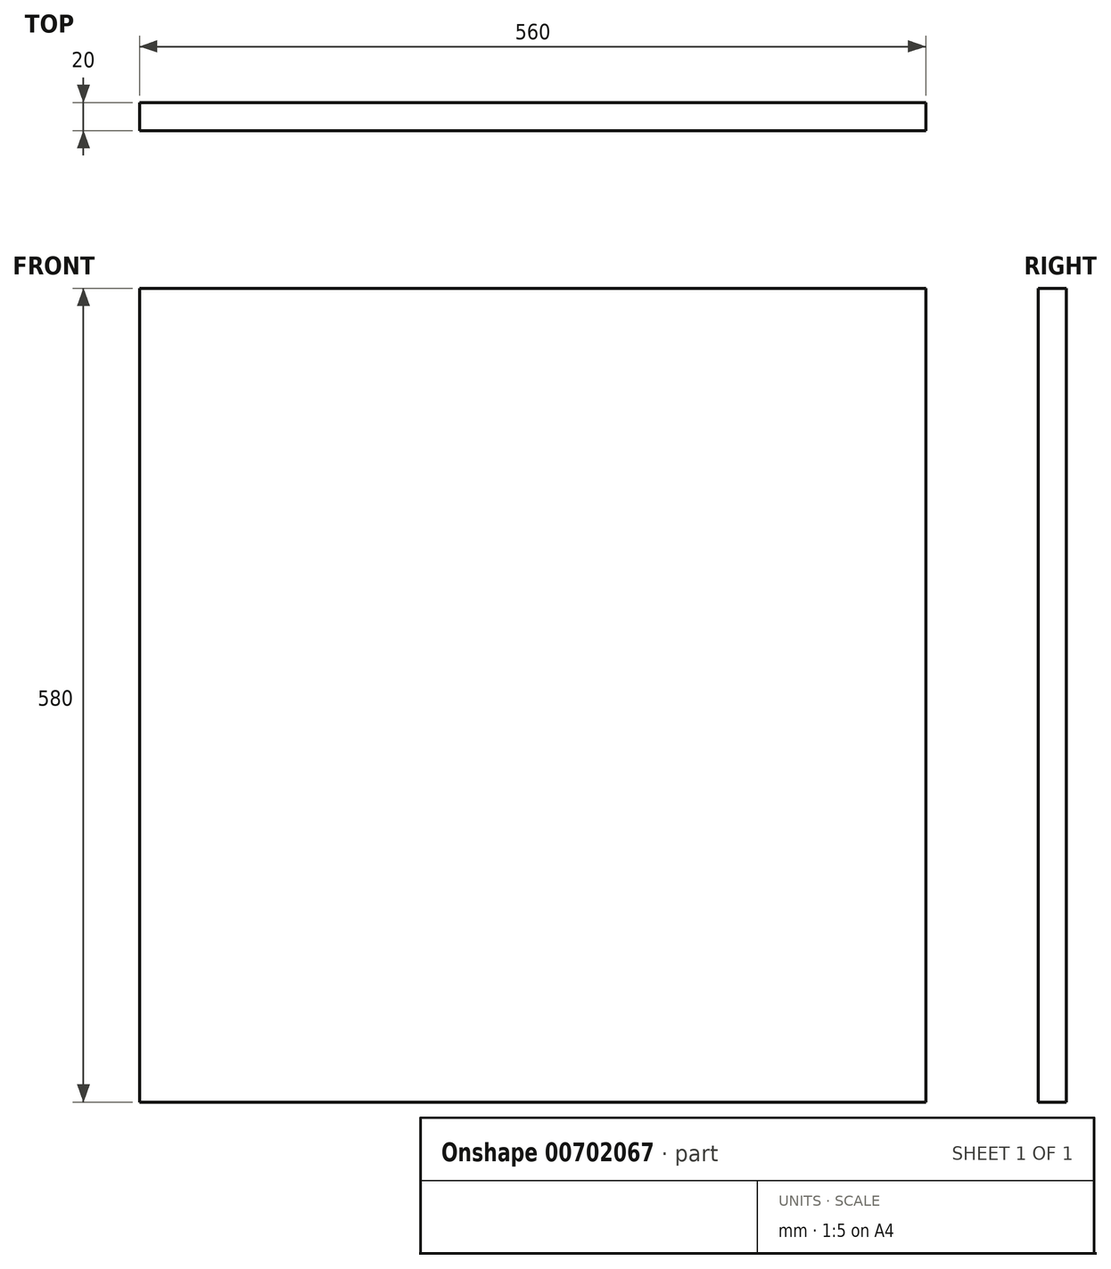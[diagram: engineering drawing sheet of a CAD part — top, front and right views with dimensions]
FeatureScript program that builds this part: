
annotation { "Feature Type Name" : "Feature", "Feature Type Description" : "" }
export const myFeature = defineFeature(function(context is Context, id is Id, definition is map)
    precondition{}
    {
        {
            var Q0;
            Q0=qCreatedBy(makeId("Front.planeOp"),FACE);
            var sketch = newSketch(context, id + "F0", { "sketchPlane" : qUnion([Q0])});
            skLineSegment(sketch, "E0.bottom", {"start": v(0, 0) * mm, "end": v(560, 0) * mm});
            skLineSegment(sketch, "E0.top", {"start": v(0, 580) * mm, "end": v(560, 580) * mm});
            skLineSegment(sketch, "E0.left", {"start": v(0, 0) * mm, "end": v(0, 580) * mm});
            skLineSegment(sketch, "E0.right", {"start": v(560, 0) * mm, "end": v(560, 580) * mm});
            skSolve(sketch);
        }
        {
            var Q0;
            Q0 = qSketchRegion(id + "F0", true);
            extrude(context, id + "F1", {"entities" : qUnion([Q0]), "depth" : 20 * mm, "offsetDistance" : 25 * mm});
        }
    });
